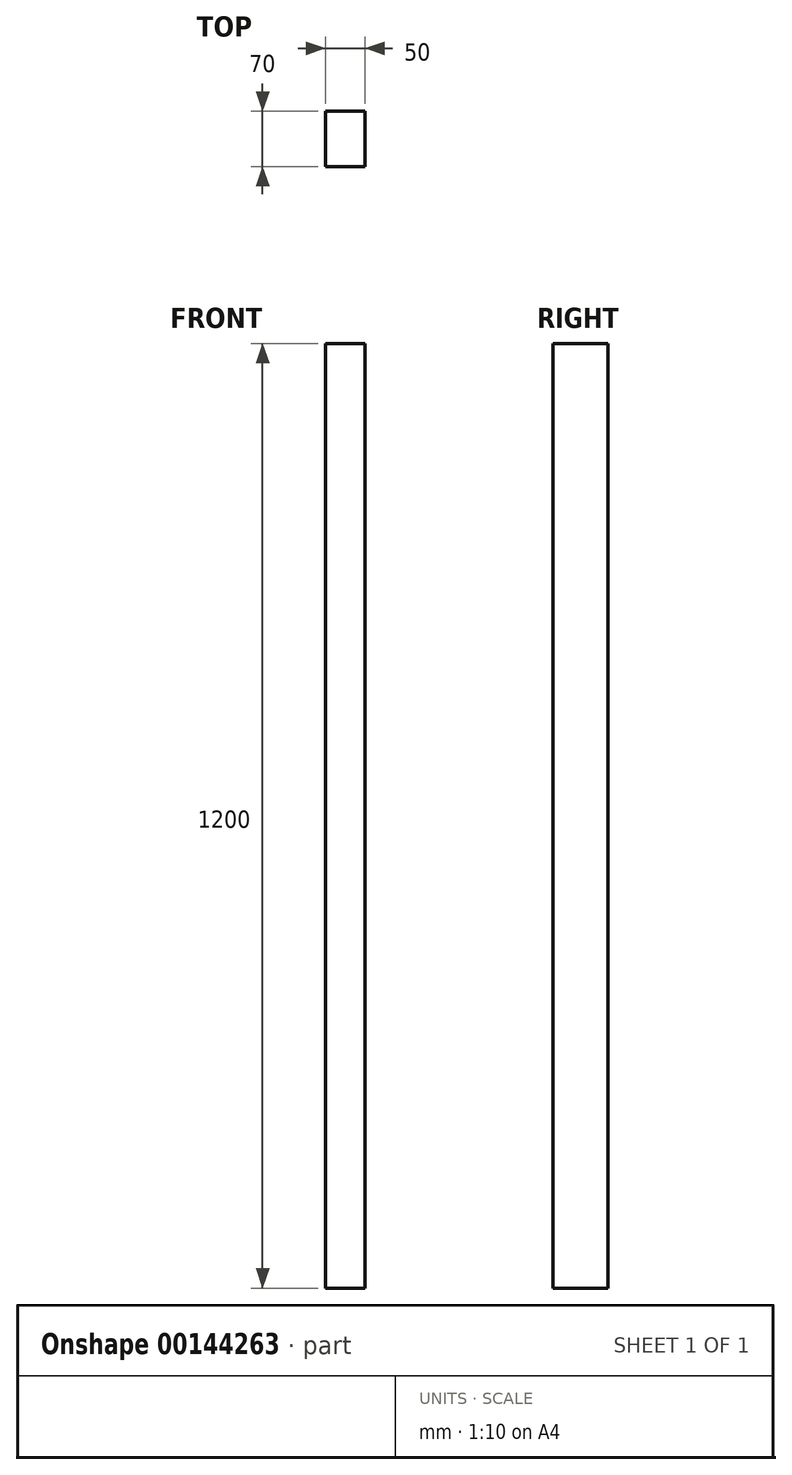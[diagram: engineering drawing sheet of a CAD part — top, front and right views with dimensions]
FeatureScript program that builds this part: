
annotation { "Feature Type Name" : "Feature", "Feature Type Description" : "" }
export const myFeature = defineFeature(function(context is Context, id is Id, definition is map)
    precondition{}
    {
        {
            var Q0;
            Q0=qCreatedBy(makeId("Top.planeOp"),FACE);
            var sketch = newSketch(context, id + "F0", { "sketchPlane" : qUnion([Q0])});
            skLineSegment(sketch, "E0.bottom", {"start": v(0, -70) * mm, "end": v(-50, -70) * mm});
            skLineSegment(sketch, "E0.top", {"start": v(0, 0) * mm, "end": v(-50, 0) * mm});
            skLineSegment(sketch, "E0.left", {"start": v(0, -70) * mm, "end": v(0, 0) * mm});
            skLineSegment(sketch, "E0.right", {"start": v(-50, -70) * mm, "end": v(-50, 0) * mm});
            skSolve(sketch);
        }
        {
            var Q0;
            Q0=makeQuery(id+"F0.imprint","IMPRINT",FACE,{"disambiguationData":[TD([[makeQuery(id+"F0.imprint","IMPRINT",EDGE,{"derivedFrom":sQuery(id+"F0.wireOp",EDGE,"E0.bottom")}),-1.0]])]});
            extrude(context, id + "F1", {"entities" : qUnion([Q0]), "depth" : 1200 * mm});
        }
    });
